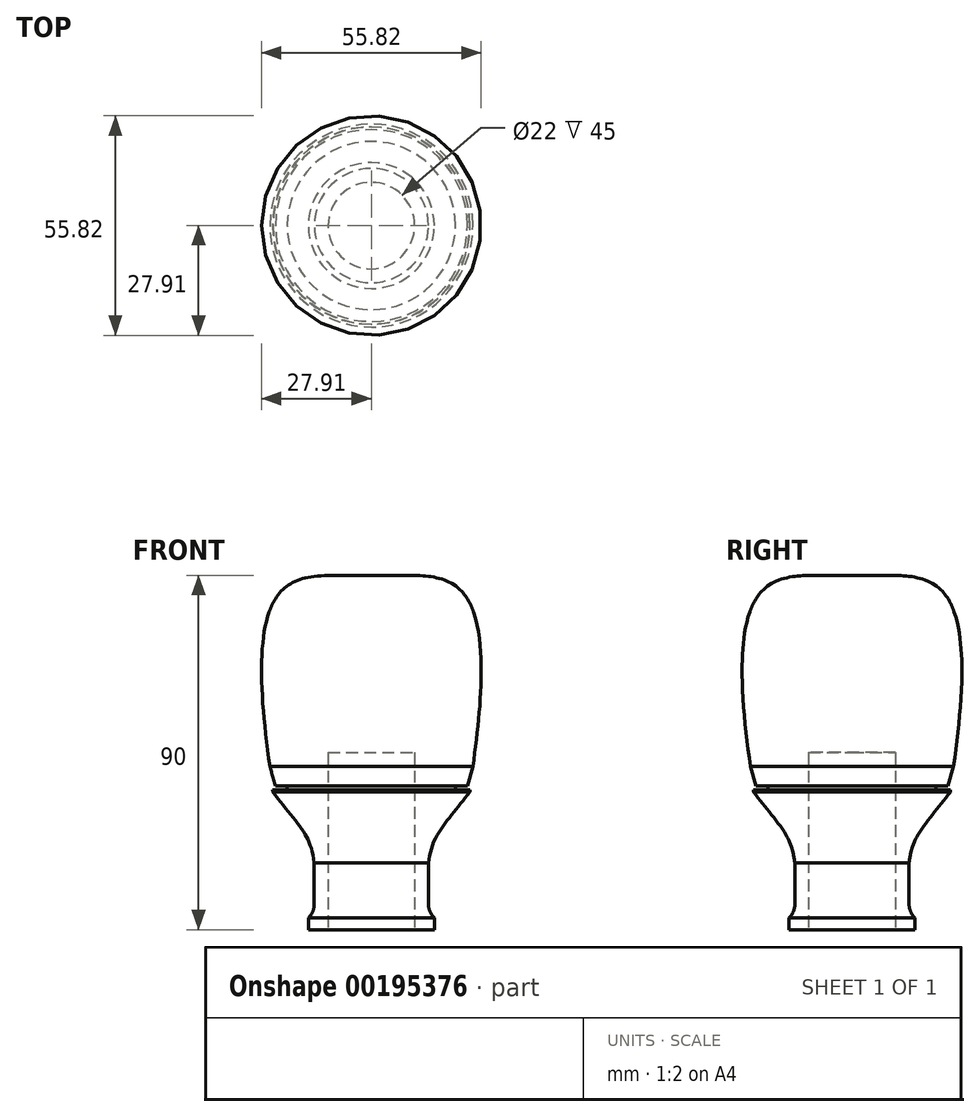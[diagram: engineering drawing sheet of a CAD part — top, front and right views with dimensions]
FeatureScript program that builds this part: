
annotation { "Feature Type Name" : "Feature", "Feature Type Description" : "" }
export const myFeature = defineFeature(function(context is Context, id is Id, definition is map)
    precondition{}
    {
        {
            var Q0;
            Q0=qCreatedBy(makeId("Front.planeOp"),FACE);
            var sketch = newSketch(context, id + "F0", { "sketchPlane" : qUnion([Q0])});
            skLineSegment(sketch, "E0", {"start": v(0, 0) * mm, "end": v(0, 82.59) * mm, "construction": true});
            skLineSegment(sketch, "E1", {"start": v(-16, 0) * mm, "end": v(-11, 0) * mm});
            skLineSegment(sketch, "E2", {"start": v(-11, 0) * mm, "end": v(-11, 45) * mm});
            skLineSegment(sketch, "E3", {"start": v(-11, 45) * mm, "end": v(0, 45) * mm});
            skLineSegment(sketch, "E4", {"start": v(-16, 0) * mm, "end": v(-16, 3) * mm});
            skLineSegment(sketch, "E5", {"start": v(-16, 3) * mm, "end": v(-14.5, 3) * mm});
            skLineSegment(sketch, "E6", {"start": v(-14.5, 3) * mm, "end": v(-14.5, 17) * mm});
            skLineSegment(sketch, "E7", {"start": v(-11, 90) * mm, "end": v(0, 90) * mm});
            skFitSpline(sketch, "E8", {"points": [v(-14.5, 17) * mm, v(-17.57, 25.4) * mm, v(-25, 35) * mm], "startDerivative": vector(-3.34, 25.01) * mm, "endDerivative": vector(-14.52, 19.22) * mm});
            skArc(sketch, "E9.filletArc", {"start": v(-25, 35.07) * mm, "mid": v(-24.99, 35) * mm, "end": v(-24.96, 34.95) * mm});
            skFitSpline(sketch, "E10", {"points": [v(-11, 90) * mm, v(-25.95, 80.77) * mm, v(-24.8, 35.07) * mm], "startDerivative": vector(-68.2, 0) * mm, "endDerivative": vector(14.55, -90.33) * mm});
            skFitSpline(sketch, "E11", {"points": [v(-25, 35.07) * mm, v(-25.95, 80.77) * mm, v(-11, 90) * mm], "startDerivative": vector(-14.08, 89.46) * mm, "endDerivative": vector(68.2, 0) * mm});
            skLineSegment(sketch, "E12.trimOffspring", {"start": v(-24.71, 83.55) * mm, "end": v(-24.71, 83.55) * mm});
            skLineSegment(sketch, "E13", {"start": v(-25, 35.07) * mm, "end": v(-25.08, 35.55) * mm});
            skLineSegment(sketch, "E14", {"start": v(-25.08, 35.55) * mm, "end": v(-24.08, 35.55) * mm});
            skLineSegment(sketch, "E15", {"start": v(-24.36, 36.55) * mm, "end": v(-26.12, 42.67) * mm});
            skFitSpline(sketch, "E16.trimOffspring", {"points": [v(-25, 35.07) * mm, v(-25.95, 80.77) * mm, v(-11, 90) * mm], "startDerivative": vector(-14.08, 89.46) * mm, "endDerivative": vector(68.2, 0) * mm});
            skLineSegment(sketch, "E17", {"start": v(0, 90) * mm, "end": v(0, 45) * mm});
            skLineSegment(sketch, "E18", {"start": v(-24.36, 36.55) * mm, "end": v(-21.36, 36.55) * mm});
            skLineSegment(sketch, "E19", {"start": v(-21.36, 36.55) * mm, "end": v(-21.36, 35.55) * mm});
            skLineSegment(sketch, "E20", {"start": v(-24.08, 35.55) * mm, "end": v(-21.36, 35.55) * mm});
            skSolve(sketch);
        }
        {
            var Q0;
            Q0=makeQuery(id+"F0.imprint","IMPRINT",FACE,{"disambiguationData":[TD([[makeQuery(id+"F0.imprint","IMPRINT",EDGE,{"derivedFrom":sQuery(id+"F0.wireOp",EDGE,"E1")}),1.0]])]});
            var Q1;
            Q1=sQuery(id+"F0.wireOp",EDGE,"E0");
            revolve(context, id + "F1", {"entities" : qUnion([Q0]), "axis" : qUnion([Q1]), "revolveType" : RevolveType.FULL});
        }
        {
            var Q0;
            Q0=makeQuery(id+"F1.opRevolve","SWEPT_EDGE",EDGE,{"disambiguationData":[OSD([sQuery(id+"F0.wireOp",EDGE,"E5"),sQuery(id+"F0.wireOp",EDGE,"E6")])]});
            fillet(context, id + "F2", {"entities" : qUnion([Q0]), "radius" : 5.08 * mm, "tangentPropagation" : true, "allowEdgeOverflow" : false});
        }
    });
